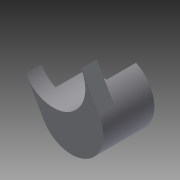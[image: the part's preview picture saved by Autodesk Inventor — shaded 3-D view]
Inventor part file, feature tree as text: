
AUTODESK INVENTOR PART (.ipt)
format: ipt  version: 2015 SP1 (Build 190203100, 203)  size: 95,232 bytes
history: native  units: in
note: dims shown in document units (in); Inventor stores cm internally (conversion verified against a paired STEP export)
features: extrude x2, sketch x2, reference x2, plane x1
ambient origin geometry x8: Origin, YZ Plane, XZ Plane, XY Plane, X Axis, Y Axis, Z Axis, Center Point
bodies: Solid1 (feature_tree)
feature tree (7):
  plane  "Work Plane1"
  extrude  "Extrusion1"  Depth=0.3543in TaperAngle=0.0deg
  extrude  "Extrusion3"  [1 undecoded]
  sketch  "Sketch1"  dims[d0=0.1575in d1=0.0in d4=0.3543in d5=0.0in]
  reference  "Reference1"
  reference  "Reference2"
  sketch  "Sketch2"
note: 1 required parameter value undecoded (feature->parameter linkage not recoverable at this tier; creation-order binding heuristic only, values carry confidence <= 0.55)
